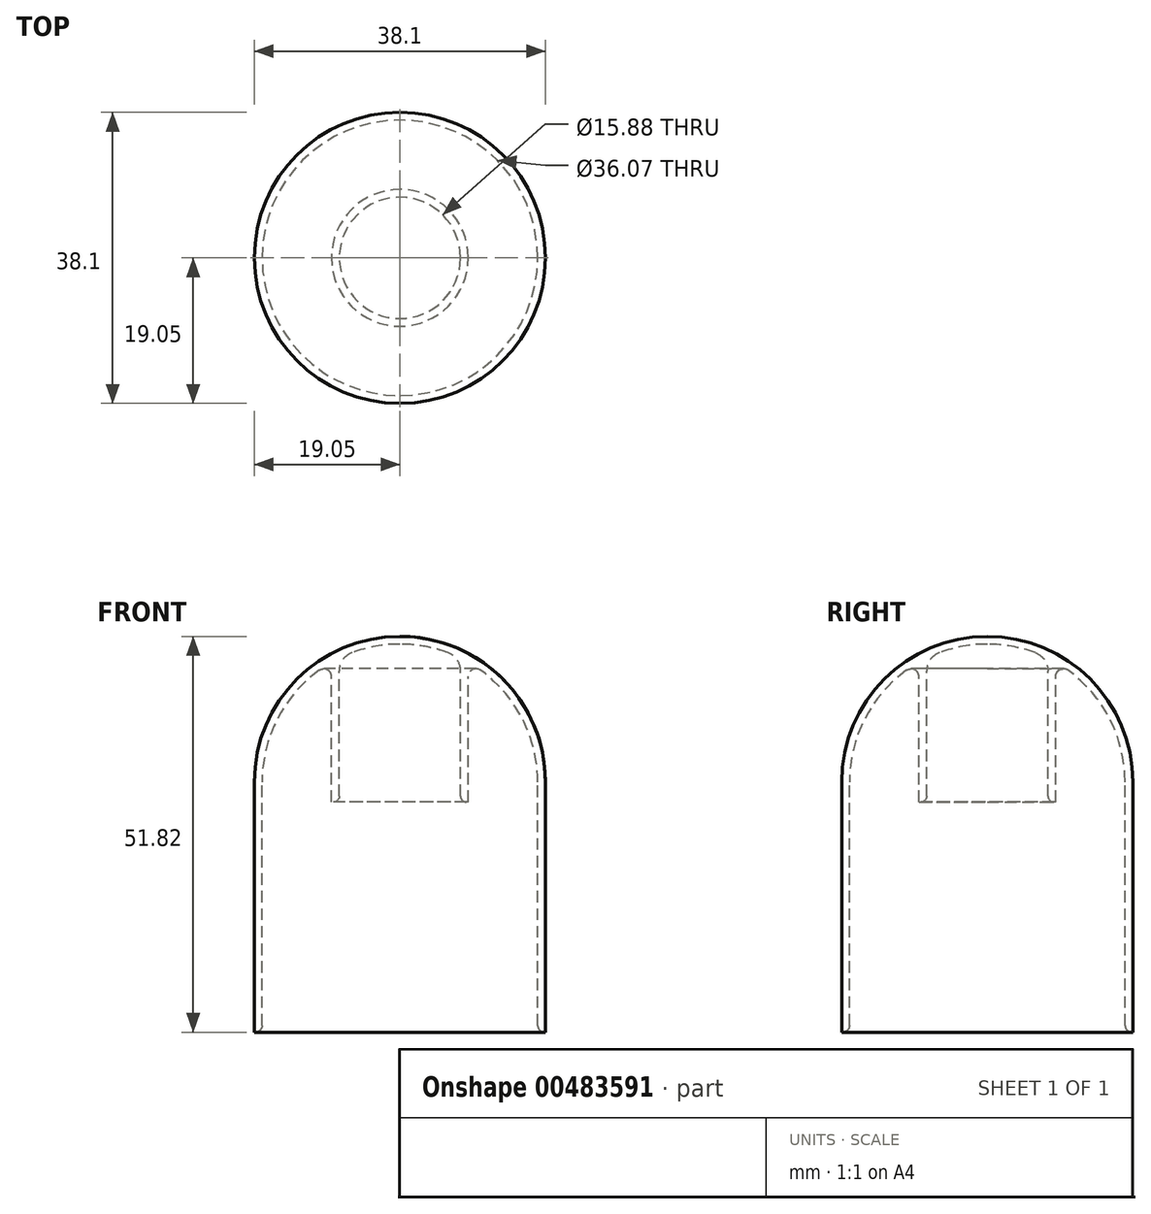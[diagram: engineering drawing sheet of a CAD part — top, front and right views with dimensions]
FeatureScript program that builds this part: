
annotation { "Feature Type Name" : "Feature", "Feature Type Description" : "" }
export const myFeature = defineFeature(function(context is Context, id is Id, definition is map)
    precondition{}
    {
        {
            var Q0;
            Q0=qCreatedBy(makeId("Front.planeOp"),FACE);
            var sketch = newSketch(context, id + "F0", { "sketchPlane" : qUnion([Q0])});
            skLineSegment(sketch, "E0", {"start": v(0, 0) * mm, "end": v(0, 67.4) * mm, "construction": true});
            skLineSegment(sketch, "E1", {"start": v(0, 67.4) * mm, "end": v(0, -87.33) * mm, "construction": true});
            skLineSegment(sketch, "E2", {"start": v(0, 0) * mm, "end": v(-79.27, 0) * mm, "construction": true});
            skLineSegment(sketch, "E3", {"start": v(-79.27, 0) * mm, "end": v(7.94, 0) * mm, "construction": true});
            skPoint(sketch, "E3.endSnap0", {"position": v(-39.63, 0) * mm});
            skArc(sketch, "E4", {"start": v(19.05, 0) * mm, "mid": v(13.47, 13.47) * mm, "end": v(0, 19.05) * mm});
            skLineSegment(sketch, "E5", {"start": v(0, 0) * mm, "end": v(7.94, 0) * mm});
            skLineSegment(sketch, "E6", {"start": v(0, 18.03) * mm, "end": v(0, 19.05) * mm});
            skLineSegment(sketch, "E7", {"start": v(19.05, 0) * mm, "end": v(19.05, -32.77) * mm});
            skLineSegment(sketch, "E8", {"start": v(18.03, -31.5) * mm, "end": v(18.03, 0) * mm});
            skArc(sketch, "E9.0", {"start": v(18.03, 0) * mm, "mid": v(16.06, 8.2) * mm, "end": v(10.56, 14.62) * mm});
            skLineSegment(sketch, "E10.trimOffspring", {"start": v(0, 0) * mm, "end": v(-19.05, 0) * mm});
            skLineSegment(sketch, "E11", {"start": v(19.05, -32.77) * mm, "end": v(18.92, -32.77) * mm});
            skLineSegment(sketch, "E12", {"start": v(18.03, -31.88) * mm, "end": v(18.03, -31.5) * mm});
            skPoint(sketch, "E13.visualSharp", {"position": v(18.03, -32.77) * mm});
            skArc(sketch, "E13.filletArc", {"start": v(18.03, -31.88) * mm, "mid": v(18.3, -32.5) * mm, "end": v(18.92, -32.77) * mm});
            skLineSegment(sketch, "E14", {"start": v(8.95, -2.63) * mm, "end": v(8.7, -2.63) * mm});
            skLineSegment(sketch, "E15", {"start": v(8.95, -2.63) * mm, "end": v(8.95, 13.8) * mm});
            skLineSegment(sketch, "E16", {"start": v(7.94, -1.87) * mm, "end": v(7.94, 14.52) * mm});
            skLineSegment(sketch, "E17.trimOffspring", {"start": v(19.05, 0) * mm, "end": v(121.38, 0) * mm, "construction": true});
            skPoint(sketch, "E18.visualSharp", {"position": v(7.94, -2.63) * mm});
            skArc(sketch, "E18.filletArc", {"start": v(7.94, -1.87) * mm, "mid": v(8.16, -2.4) * mm, "end": v(8.7, -2.63) * mm});
            skArc(sketch, "E19.trimOffspring", {"start": v(6.28, 16.9) * mm, "mid": v(3.2, 17.75) * mm, "end": v(0, 18.03) * mm});
            skPoint(sketch, "E20.visualSharp", {"position": v(8.95, 15.65) * mm});
            skArc(sketch, "E20.filletArc", {"start": v(10.56, 14.62) * mm, "mid": v(9.5, 14.7) * mm, "end": v(8.95, 13.8) * mm});
            skPoint(sketch, "E21.visualSharp", {"position": v(7.94, 16.2) * mm});
            skArc(sketch, "E21.filletArc", {"start": v(7.94, 14.52) * mm, "mid": v(7.48, 15.97) * mm, "end": v(6.28, 16.9) * mm});
            skSolve(sketch);
        }
        {
            var Q0;
            Q0=makeQuery(id+"F0.imprint","IMPRINT",FACE,{"disambiguationData":[TD([[makeQuery(id+"F0.imprint","IMPRINT",EDGE,{"derivedFrom":sQuery(id+"F0.wireOp",EDGE,"E4")}),1.0]])]});
            var Q1;
            Q1=sQuery(id+"F0.wireOp",EDGE,"E1");
            revolve(context, id + "F1", {"entities" : qUnion([Q0]), "axis" : qUnion([Q1]), "revolveType" : RevolveType.FULL});
        }
    });
